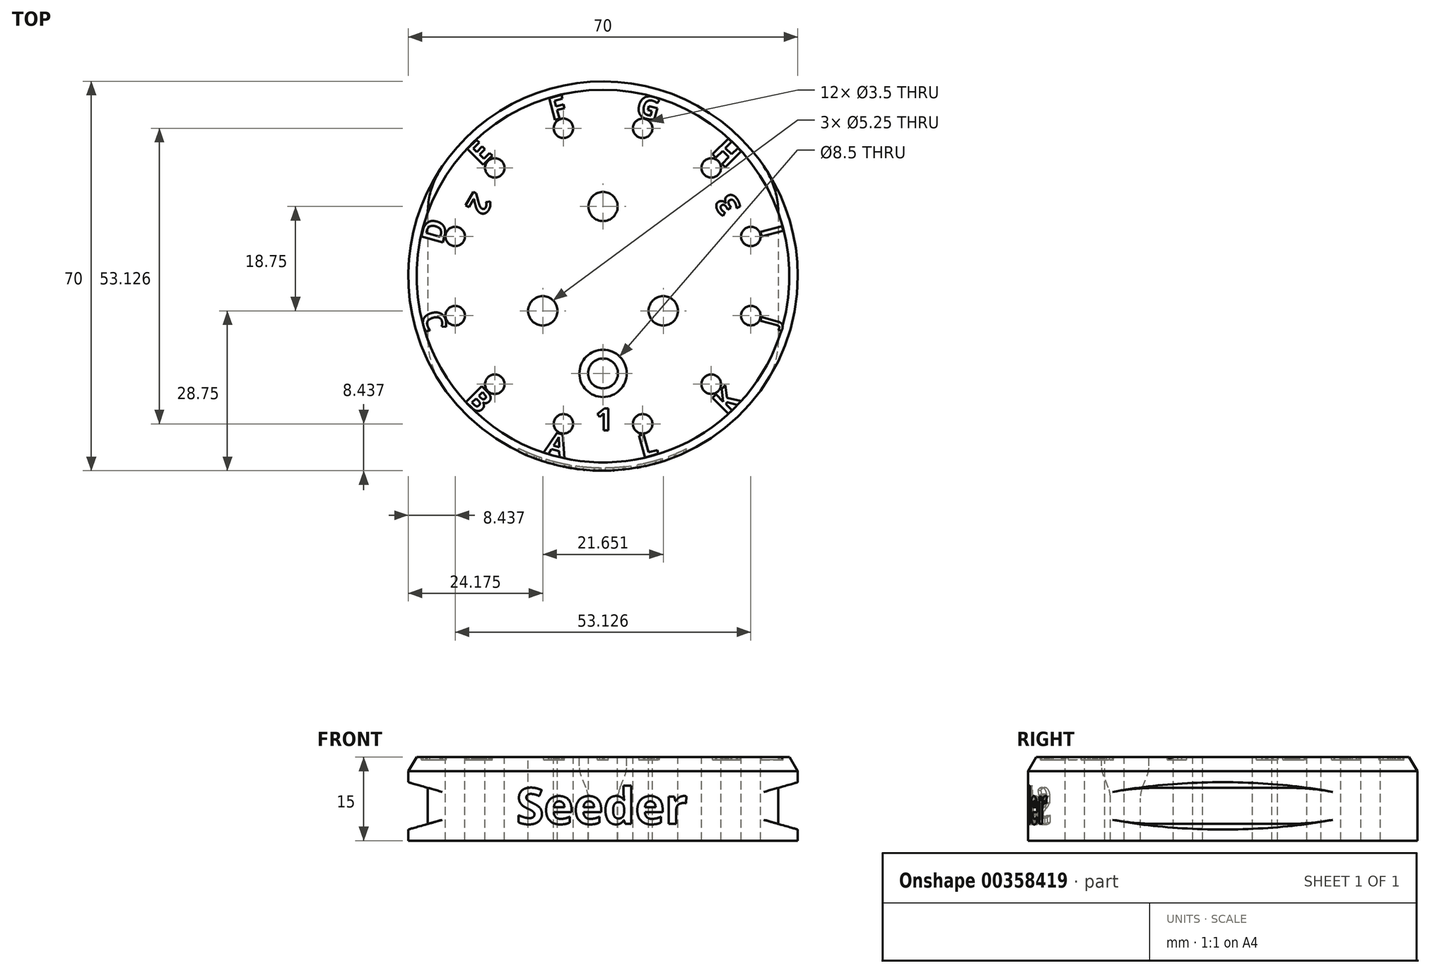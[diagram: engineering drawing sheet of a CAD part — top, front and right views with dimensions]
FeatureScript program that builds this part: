
annotation { "Feature Type Name" : "Feature", "Feature Type Description" : "" }
export const myFeature = defineFeature(function(context is Context, id is Id, definition is map)
    precondition{}
    {
        {
            var Q0;
            Q0=qCreatedBy(makeId("Top.planeOp"),FACE);
            var sketch = newSketch(context, id + "F0", { "sketchPlane" : qUnion([Q0])});
            skCircle(sketch, "E0", {"center": v(0, 0) * mm, "radius": 35 * mm});
            skSolve(sketch);
        }
        {
            var Q0;
            Q0=qSketchRegion(id+"F0",true);
            extrude(context, id + "F1", {"entities" : qUnion([Q0]), "depth" : 15 * mm});
        }
        {
            var Q0;
            Q0=qCreatedBy(makeId("Front.planeOp"),FACE);
            var sketch = newSketch(context, id + "F2", { "sketchPlane" : qUnion([Q0])});
            skText(sketch, "E1", { "text": "Seeder", "fontName": "OpenSans-Bold.ttf"});
            const initialGuessF2  = {"E1": [-0.0156, 0.003, 1, 0, 0.0065]};
            skSetInitialGuess(sketch, initialGuessF2);
            skSolve(sketch);
        }
        {
            var Q0;
            Q0=qSketchRegion(id+"F2",true);
            var Q1;
            Q1=makeQuery(id+"F1.opExtrude","SWEPT_FACE",FACE,{"disambiguationData":[OSD([sQuery(id+"F0.wireOp",EDGE,"E0")])]});
            extrude(context, id + "F3", {"entities" : qUnion([Q0]), "operationType" : NewBodyOperationType.REMOVE, "endBound" : BoundingType.THROUGH_ALL, "endBoundEntityFace" : qUnion([Q1]), "depth" : 25 * mm});
        }
        {
            var Q0;
            Q0=makeQuery(id+"F1.opExtrude","CAP_FACE",FACE,{"disambiguationData":[OSD([sQuery(id+"F0.wireOp",EDGE,"E0")])],"isStart":false});
            var sketch = newSketch(context, id + "F4", { "sketchPlane" : qUnion([Q0])});
            skCircle(sketch, "E2", {"center": v(0, 0) * mm, "radius": 34.5 * mm});
            skSolve(sketch);
        }
        {
            var Q0;
            Q0=qSketchRegion(id+"F4",true);
            var Q1;
            Q1=makeQuery(id+"F1.opExtrude","CAP_FACE",FACE,{"disambiguationData":[OSD([sQuery(id+"F0.wireOp",EDGE,"E0")])],"isStart":true});
            extrude(context, id + "F5", {"entities" : qUnion([Q0]), "operationType" : NewBodyOperationType.ADD, "endBound" : BoundingType.UP_TO_SURFACE, "oppositeDirection" : true, "endBoundEntityFace" : qUnion([Q1]), "depth" : 25 * mm});
        }
        {
            var Q0;
            Q0=qCreatedBy(makeId("Front.planeOp"),FACE);
            var sketch = newSketch(context, id + "F6", { "sketchPlane" : qUnion([Q0])});
            skLineSegment(sketch, "E3", {"start": v(-35, 10.5) * mm, "end": v(-35, 2) * mm});
            skLineSegment(sketch, "E4", {"start": v(-35, 2) * mm, "end": v(-31.5, 3) * mm});
            skLineSegment(sketch, "E5", {"start": v(-31.5, 3) * mm, "end": v(-31.5, 9.5) * mm});
            skLineSegment(sketch, "E6", {"start": v(-31.5, 9.5) * mm, "end": v(-35, 10.5) * mm});
            skLineSegment(sketch, "E7.MirrorCS", {"start": v(35, 10.5) * mm, "end": v(35, 2) * mm});
            skLineSegment(sketch, "E8.MirrorCS", {"start": v(31.5, 9.5) * mm, "end": v(35, 10.5) * mm});
            skLineSegment(sketch, "E9.MirrorCS", {"start": v(35, 2) * mm, "end": v(31.5, 3) * mm});
            skLineSegment(sketch, "E10.MirrorCS", {"start": v(31.5, 3) * mm, "end": v(31.5, 9.5) * mm});
            skSolve(sketch);
        }
        {
            var Q0;
            Q0=qSketchRegion(id+"F6",true);
            extrude(context, id + "F7", {"entities" : qUnion([Q0]), "operationType" : NewBodyOperationType.REMOVE, "endBound" : BoundingType.THROUGH_ALL, "oppositeDirection" : true, "depth" : 25 * mm, "hasSecondDirection" : true, "secondDirectionBound" : BoundingType.THROUGH_ALL, "secondDirectionOppositeDirection" : false, "secondDirectionDepth" : 25 * mm});
        }
        {
            var Q0;
            {var subQ0=sQuery(id+"F0.wireOp",EDGE,"E0");Q0=makeQuery(id+"F7.boolean.opBoolean","INTERSECT",EDGE,{"disambiguationData":[OD(0.0)],"derivedFrom":[makeQuery(id+"F3.boolean.opBoolean","SPLIT",FACE,{"disambiguationData":[TD([makeQuery(id+"F1.opExtrude","CAP_FACE",FACE,{"disambiguationData":[OSD([subQ0])],"isStart":true})])],"derivedFrom":makeQuery(id+"F1.opExtrude","SWEPT_FACE",FACE,{"disambiguationData":[OSD([subQ0])]})}),makeQuery(id+"F7.opExtrude","SWEPT_FACE",FACE,{"disambiguationData":[OSD([sQuery(id+"F6.wireOp",EDGE,"E5")])]})]});}
            var Q1;
            {var subQ0=sQuery(id+"F0.wireOp",EDGE,"E0");Q1=makeQuery(id+"F7.boolean.opBoolean","INTERSECT",EDGE,{"disambiguationData":[OD(0.0)],"derivedFrom":[makeQuery(id+"F3.boolean.opBoolean","SPLIT",FACE,{"disambiguationData":[TD([makeQuery(id+"F1.opExtrude","CAP_FACE",FACE,{"disambiguationData":[OSD([subQ0])],"isStart":true})])],"derivedFrom":makeQuery(id+"F1.opExtrude","SWEPT_FACE",FACE,{"disambiguationData":[OSD([subQ0])]})}),makeQuery(id+"F7.opExtrude","SWEPT_FACE",FACE,{"disambiguationData":[OSD([sQuery(id+"F6.wireOp",EDGE,"E10.MirrorCS")])]})]});}
            var Q2;
            {var subQ0=sQuery(id+"F0.wireOp",EDGE,"E0");Q2=makeQuery(id+"F7.boolean.opBoolean","INTERSECT",EDGE,{"disambiguationData":[OD(1.0)],"derivedFrom":[makeQuery(id+"F3.boolean.opBoolean","SPLIT",FACE,{"disambiguationData":[TD([makeQuery(id+"F1.opExtrude","CAP_FACE",FACE,{"disambiguationData":[OSD([subQ0])],"isStart":true})])],"derivedFrom":makeQuery(id+"F1.opExtrude","SWEPT_FACE",FACE,{"disambiguationData":[OSD([subQ0])]})}),makeQuery(id+"F7.opExtrude","SWEPT_FACE",FACE,{"disambiguationData":[OSD([sQuery(id+"F6.wireOp",EDGE,"E10.MirrorCS")])]})]});}
            var Q3;
            {var subQ0=sQuery(id+"F0.wireOp",EDGE,"E0");Q3=makeQuery(id+"F7.boolean.opBoolean","INTERSECT",EDGE,{"disambiguationData":[OD(1.0)],"derivedFrom":[makeQuery(id+"F3.boolean.opBoolean","SPLIT",FACE,{"disambiguationData":[TD([makeQuery(id+"F1.opExtrude","CAP_FACE",FACE,{"disambiguationData":[OSD([subQ0])],"isStart":true})])],"derivedFrom":makeQuery(id+"F1.opExtrude","SWEPT_FACE",FACE,{"disambiguationData":[OSD([subQ0])]})}),makeQuery(id+"F7.opExtrude","SWEPT_FACE",FACE,{"disambiguationData":[OSD([sQuery(id+"F6.wireOp",EDGE,"E5")])]})]});}
            fillet(context, id + "F8", {"entities" : qUnion([Q0, Q1, Q2, Q3]), "radius" : 15 * mm, "tangentPropagation" : true, "allowEdgeOverflow" : false});
        }
        {
            var Q0;
            Q0=makeQuery(id+"F1.opExtrude","CAP_FACE",FACE,{"disambiguationData":[OSD([sQuery(id+"F0.wireOp",EDGE,"E0")])],"isStart":false});
            var sketch = newSketch(context, id + "F9", { "sketchPlane" : qUnion([Q0])});
            skCircle(sketch, "E11", {"center": v(0, 12.5) * mm, "radius": 2.62 * mm});
            skCircle(sketch, "E12.1.0", {"center": v(-10.83, -6.25) * mm, "radius": 2.62 * mm});
            skCircle(sketch, "E12.2.0", {"center": v(10.83, -6.25) * mm, "radius": 2.62 * mm});
            skPoint(sketch, "E12.center", {"position": v(0, 0) * mm});
            skCircle(sketch, "E13", {"center": v(0, 0) * mm, "radius": 12.5 * mm, "construction": true});
            skSolve(sketch);
        }
        {
            var Q0;
            Q0=qSketchRegion(id+"F9",true);
            extrude(context, id + "F10", {"entities" : qUnion([Q0]), "operationType" : NewBodyOperationType.REMOVE, "endBound" : BoundingType.THROUGH_ALL, "oppositeDirection" : true, "depth" : 25 * mm});
        }
        {
            var Q0;
            Q0=makeQuery(id+"F1.opExtrude","CAP_FACE",FACE,{"disambiguationData":[OSD([sQuery(id+"F0.wireOp",EDGE,"E0")])],"isStart":false});
            var sketch = newSketch(context, id + "F11", { "sketchPlane" : qUnion([Q0])});
            skCircle(sketch, "E14", {"center": v(0, -17.5) * mm, "radius": 2.68 * mm});
            skCircle(sketch, "E15", {"center": v(0, 0) * mm, "radius": 17.5 * mm, "construction": true});
            skSolve(sketch);
        }
        {
            var Q0;
            Q0=qSketchRegion(id+"F11",true);
            extrude(context, id + "F12", {"entities" : qUnion([Q0]), "operationType" : NewBodyOperationType.REMOVE, "endBound" : BoundingType.THROUGH_ALL, "oppositeDirection" : true, "depth" : 25 * mm});
        }
        {
            var Q0;
            Q0=makeQuery(id+"F1.opExtrude","CAP_FACE",FACE,{"disambiguationData":[OSD([sQuery(id+"F0.wireOp",EDGE,"E0")])],"isStart":false});
            var sketch = newSketch(context, id + "F13", { "sketchPlane" : qUnion([Q0])});
            skCircle(sketch, "E16", {"center": v(0, -17.5) * mm, "radius": 4.25 * mm});
            skSolve(sketch);
        }
        {
            var Q0;
            Q0=qSketchRegion(id+"F13",true);
            extrude(context, id + "F14", {"entities" : qUnion([Q0]), "operationType" : NewBodyOperationType.REMOVE, "oppositeDirection" : true, "depth" : 7.5 * mm});
        }
        {
            var Q0;
            Q0=makeQuery(id+"F14.boolean.opBoolean","COPY",EDGE,{"derivedFrom":makeQuery(id+"F14.opExtrude","CAP_EDGE",EDGE,{"disambiguationData":[OSD([sQuery(id+"F13.wireOp",EDGE,"E16")])],"isStart":false})});
            chamfer(context, id + "F15", {"entities" : qUnion([Q0]), "chamferType" : ChamferType.TWO_OFFSETS, "width1" : 5 * mm, "oppositeDirection" : true, "width2" : 2 * mm, "tangentPropagation" : true});
        }
        {
            var Q0;
            {var subQ0=sQuery(id+"F13.wireOp",EDGE,"E16");Q0=makeQuery(id+"F15.opChamfer","BLEND_EDGE",EDGE,{"blendedFrom":[makeQuery(id+"F14.boolean.opBoolean","COPY",EDGE,{"derivedFrom":makeQuery(id+"F14.opExtrude","CAP_EDGE",EDGE,{"disambiguationData":[OSD([subQ0])],"isStart":false})}),makeQuery(id+"F14.boolean.opBoolean","COPY",FACE,{"derivedFrom":makeQuery(id+"F14.opExtrude","SWEPT_FACE",FACE,{"disambiguationData":[OSD([subQ0])]})})],"blendedInto":[makeQuery(id+"F14.boolean.opBoolean","COPY",FACE,{"derivedFrom":makeQuery(id+"F14.opExtrude","SWEPT_FACE",FACE,{"disambiguationData":[OSD([subQ0])]})})]});}
            var Q1;
            Q1=makeQuery(id+"F15.opChamfer","BLEND_EDGE",EDGE,{"blendedFrom":[makeQuery(id+"F14.boolean.opBoolean","COPY",EDGE,{"derivedFrom":makeQuery(id+"F14.opExtrude","CAP_EDGE",EDGE,{"disambiguationData":[OSD([sQuery(id+"F13.wireOp",EDGE,"E16")])],"isStart":false})}),makeQuery(id+"F12.boolean.opBoolean","COPY",FACE,{"derivedFrom":makeQuery(id+"F12.opExtrude","SWEPT_FACE",FACE,{"disambiguationData":[OSD([sQuery(id+"F11.wireOp",EDGE,"E14")])]})})],"blendedInto":[makeQuery(id+"F12.boolean.opBoolean","COPY",FACE,{"derivedFrom":makeQuery(id+"F12.opExtrude","SWEPT_FACE",FACE,{"disambiguationData":[OSD([sQuery(id+"F11.wireOp",EDGE,"E14")])]})})]});
            fillet(context, id + "F16", {"entities" : qUnion([Q0, Q1]), "radius" : 5 * mm, "tangentPropagation" : true, "allowEdgeOverflow" : false});
        }
        {
            var Q0;
            Q0=makeQuery(id+"F1.opExtrude","CAP_FACE",FACE,{"disambiguationData":[OSD([sQuery(id+"F0.wireOp",EDGE,"E0")])],"isStart":false});
            var sketch = newSketch(context, id + "F17", { "sketchPlane" : qUnion([Q0])});
            skCircle(sketch, "E17", {"center": v(19.45, 19.45) * mm, "radius": 1.75 * mm});
            skCircle(sketch, "E18", {"center": v(0, 0) * mm, "radius": 27.5 * mm, "construction": true});
            skLineSegment(sketch, "E19", {"start": v(0, 0) * mm, "end": v(19.45, 19.45) * mm, "construction": true});
            skCircle(sketch, "E20.1.1", {"center": v(7.12, 26.56) * mm, "radius": 1.75 * mm});
            skCircle(sketch, "E20.2.1", {"center": v(-7.12, 26.56) * mm, "radius": 1.75 * mm});
            skCircle(sketch, "E20.3.1", {"center": v(-19.45, 19.45) * mm, "radius": 1.75 * mm});
            skCircle(sketch, "E20.4.1", {"center": v(-26.56, 7.12) * mm, "radius": 1.75 * mm});
            skCircle(sketch, "E20.5.1", {"center": v(-26.56, -7.12) * mm, "radius": 1.75 * mm});
            skCircle(sketch, "E20.6.1", {"center": v(-19.45, -19.45) * mm, "radius": 1.75 * mm});
            skCircle(sketch, "E20.7.1", {"center": v(-7.12, -26.56) * mm, "radius": 1.75 * mm});
            skCircle(sketch, "E20.8.1", {"center": v(7.12, -26.56) * mm, "radius": 1.75 * mm});
            skCircle(sketch, "E20.9.1", {"center": v(19.45, -19.45) * mm, "radius": 1.75 * mm});
            skCircle(sketch, "E20.10.1", {"center": v(26.56, -7.12) * mm, "radius": 1.75 * mm});
            skCircle(sketch, "E20.11.1", {"center": v(26.56, 7.12) * mm, "radius": 1.75 * mm});
            skSolve(sketch);
        }
        {
            var Q0;
            Q0=qSketchRegion(id+"F17",true);
            extrude(context, id + "F18", {"entities" : qUnion([Q0]), "operationType" : NewBodyOperationType.REMOVE, "endBound" : BoundingType.THROUGH_ALL, "oppositeDirection" : true, "depth" : 25 * mm});
        }
        {
            var Q0;
            Q0=makeQuery(id+"F1.opExtrude","CAP_EDGE",EDGE,{"disambiguationData":[OSD([sQuery(id+"F0.wireOp",EDGE,"E0")])],"isStart":false});
            chamfer(context, id + "F19", {"entities" : qUnion([Q0]), "chamferType" : ChamferType.TWO_OFFSETS, "width1" : 2.5 * mm, "oppositeDirection" : true, "width2" : 1.5 * mm, "tangentPropagation" : true});
        }
        {
            var Q0;
            Q0=makeQuery(id+"F1.opExtrude","CAP_FACE",FACE,{"disambiguationData":[OSD([sQuery(id+"F0.wireOp",EDGE,"E0")])],"isStart":false});
            var sketch = newSketch(context, id + "F20", { "sketchPlane" : qUnion([Q0])});
            skText(sketch, "E21", { "text": "A", "fontName": "OpenSans-Bold.ttf"});
            skText(sketch, "E22", { "text": "B", "fontName": "OpenSans-Bold.ttf"});
            skText(sketch, "E23", { "text": "C", "fontName": "OpenSans-Bold.ttf"});
            skText(sketch, "E24", { "text": "E", "fontName": "OpenSans-Bold.ttf"});
            skText(sketch, "E25", { "text": "F", "fontName": "OpenSans-Bold.ttf"});
            skText(sketch, "E26", { "text": "G", "fontName": "OpenSans-Bold.ttf"});
            skText(sketch, "E27", { "text": "H", "fontName": "OpenSans-Bold.ttf"});
            skText(sketch, "E28", { "text": "I", "fontName": "OpenSans-Bold.ttf"});
            skText(sketch, "E29", { "text": "J", "fontName": "OpenSans-Bold.ttf"});
            skText(sketch, "E30", { "text": "K", "fontName": "OpenSans-Bold.ttf"});
            skText(sketch, "E31", { "text": "L", "fontName": "OpenSans-Bold.ttf"});
            skText(sketch, "E32", { "text": "D", "fontName": "OpenSans-Bold.ttf"});
            skCircle(sketch, "E33", {"center": v(0, 0) * mm, "radius": 29.38 * mm, "construction": true});
            skText(sketch, "E34", { "text": "1", "fontName": "OpenSans-Bold.ttf"});
            skText(sketch, "E35", { "text": "2", "fontName": "OpenSans-Bold.ttf"});
            skText(sketch, "E36", { "text": "3", "fontName": "OpenSans-Bold.ttf"});
            skCircle(sketch, "E37", {"center": v(0, 0) * mm, "radius": 23.75 * mm, "construction": true});
            const initialGuessF20  = {"E21": [-0.0107, -0.03174, 0.96593, -0.25882, 0.00406], "E22": [-0.025, -0.02228, 0.7071, -0.7071, 0.00406], "E23": [-0.03278, -0.00684, 0.25882, -0.96593, 0.00406], "E24": [-0.0219, 0.01964, 0.7071, 0.7071, 0.00406], "E25": [-0.00914, 0.02796, 0.96593, 0.25882, 0.00406], "E26": [0.00567, 0.0289, 0.96593, -0.25882, 0.00406], "E27": [0.0193, 0.02225, 0.7071, -0.7071, 0.00406], "E28": [0.02815, 0.00844, 0.25882, -0.96593, 0.00406], "E29": [0.0313, -0.00927, 0.25882, 0.96593, 0.00325], "E30": [0.02219, -0.0251, 0.7071, 0.7071, 0.00406], "E31": [0.00703, -0.03273, 0.96593, 0.25882, 0.00406], "E32": [-0.02892, 0.00557, 0.25882, 0.96593, 0.00406], "E34": [-0.00133, -0.02775, 1, 0, 0.004], "E35": [-0.0232, 0.01533, -0.5, -0.86603, 0.004], "E36": [0.02486, 0.01244, -0.5, 0.86603, 0.004]};
            skSetInitialGuess(sketch, initialGuessF20);
            skSolve(sketch);
        }
        {
            var Q0;
            Q0=qSketchRegion(id+"F20",true);
            extrude(context, id + "F21", {"entities" : qUnion([Q0]), "operationType" : NewBodyOperationType.REMOVE, "oppositeDirection" : true, "depth" : .5 * mm});
        }
    });
